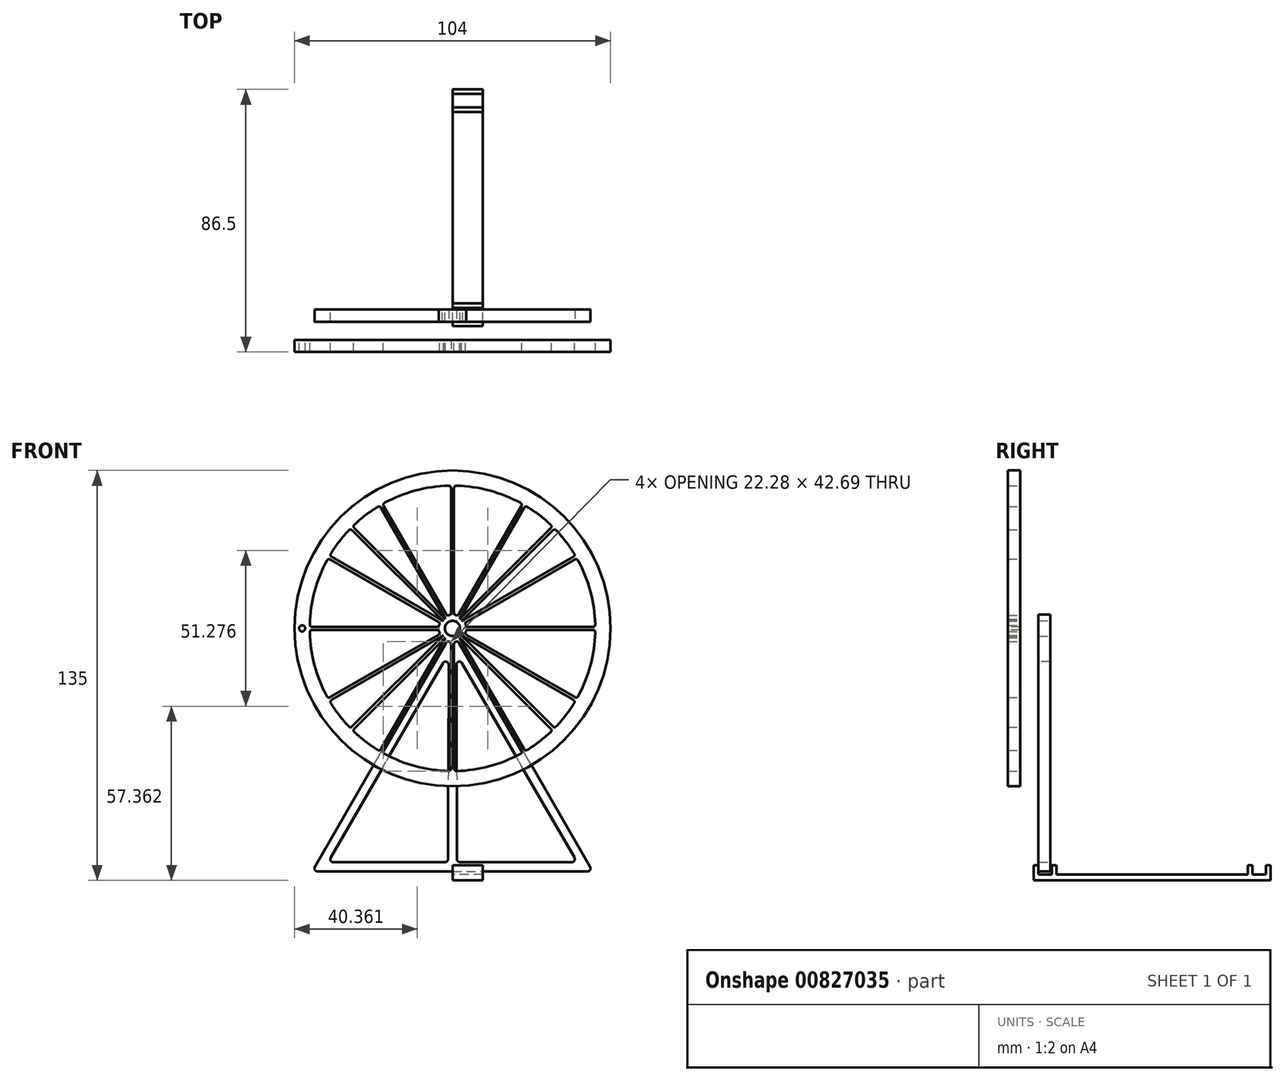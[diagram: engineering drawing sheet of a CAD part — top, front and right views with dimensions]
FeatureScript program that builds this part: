
annotation { "Feature Type Name" : "Feature", "Feature Type Description" : "" }
export const myFeature = defineFeature(function(context is Context, id is Id, definition is map)
    precondition{}
    {
        {
            var Q0;
            Q0=qCreatedBy(makeId("Front.planeOp"),FACE);
            var sketch = newSketch(context, id + "F0", { "sketchPlane" : qUnion([Q0])});
            skCircle(sketch, "E0", {"center": v(0, 0) * mm, "radius": 52 * mm});
            skCircle(sketch, "E1.0", {"center": v(0, 0) * mm, "radius": 47 * mm});
            skLineSegment(sketch, "E2", {"start": v(0, 0) * mm, "end": v(0, 47) * mm});
            skLineSegment(sketch, "E3", {"start": v(0, 0) * mm, "end": v(47, 0) * mm});
            skLineSegment(sketch, "E4", {"start": v(0, 0) * mm, "end": v(23.5, 40.7) * mm});
            skPoint(sketch, "E4.endSnap0", {"position": v(23.5, 0) * mm});
            skLineSegment(sketch, "E5", {"start": v(0, 0) * mm, "end": v(40.7, 23.5) * mm});
            skPoint(sketch, "E5.endSnap0", {"position": v(0, 23.5) * mm});
            skLineSegment(sketch, "E6", {"start": v(0, 0) * mm, "end": v(33.23, 33.23) * mm});
            skLineSegment(sketch, "E7.0", {"start": v(0.5, 1.87) * mm, "end": v(23.07, 40.95) * mm});
            skLineSegment(sketch, "E7.1", {"start": v(0.5, 1.87) * mm, "end": v(0.5, 23) * mm});
            skLineSegment(sketch, "E8.0", {"start": v(2.33, 3.04) * mm, "end": v(23.93, 40.45) * mm});
            skLineSegment(sketch, "E8.1", {"start": v(2.33, 3.04) * mm, "end": v(15.9, 16.62) * mm});
            skLineSegment(sketch, "E9.0", {"start": v(3.04, 2.33) * mm, "end": v(16.62, 15.9) * mm});
            skLineSegment(sketch, "E9.1", {"start": v(3.04, 2.33) * mm, "end": v(40.45, 23.93) * mm});
            skLineSegment(sketch, "E10.0", {"start": v(1.87, 0.5) * mm, "end": v(40.95, 23.07) * mm});
            skLineSegment(sketch, "E10.1", {"start": v(1.87, 0.5) * mm, "end": v(23, 0.5) * mm});
            skLineSegment(sketch, "E11.1.0", {"start": v(-2.31, 3.03) * mm, "end": v(-15.89, 16.6) * mm});
            skLineSegment(sketch, "E11.1.1", {"start": v(-3.02, 2.32) * mm, "end": v(-16.6, 15.9) * mm});
            skLineSegment(sketch, "E11.1.2", {"start": v(0.02, -0.01) * mm, "end": v(-23.48, 40.7) * mm});
            skLineSegment(sketch, "E11.1.3", {"start": v(-3.02, 2.32) * mm, "end": v(-40.43, 23.92) * mm});
            skLineSegment(sketch, "E11.1.4", {"start": v(0.02, -0.01) * mm, "end": v(-40.68, 23.49) * mm});
            skLineSegment(sketch, "E11.1.5", {"start": v(-1.85, 0.49) * mm, "end": v(-22.98, 0.49) * mm});
            skLineSegment(sketch, "E11.1.6", {"start": v(-0.48, 1.86) * mm, "end": v(-0.48, 22.99) * mm});
            skLineSegment(sketch, "E11.1.7", {"start": v(0.02, -0.01) * mm, "end": v(-33.21, 33.22) * mm});
            skLineSegment(sketch, "E11.1.8", {"start": v(-0.48, 1.86) * mm, "end": v(-23.05, 40.94) * mm});
            skLineSegment(sketch, "E11.1.9", {"start": v(-2.31, 3.03) * mm, "end": v(-23.91, 40.44) * mm});
            skLineSegment(sketch, "E11.1.10", {"start": v(-1.85, 0.49) * mm, "end": v(-40.93, 23.06) * mm});
            skLineSegment(sketch, "E11.2.0", {"start": v(-3, -2.32) * mm, "end": v(-16.59, -15.9) * mm});
            skLineSegment(sketch, "E11.2.1", {"start": v(-2.3, -3.03) * mm, "end": v(-15.88, -16.6) * mm});
            skLineSegment(sketch, "E11.2.2", {"start": v(0.03, 0.01) * mm, "end": v(-40.67, -23.49) * mm});
            skLineSegment(sketch, "E11.2.3", {"start": v(-2.3, -3.03) * mm, "end": v(-23.9, -40.44) * mm});
            skLineSegment(sketch, "E11.2.4", {"start": v(0.03, 0.01) * mm, "end": v(-23.47, -40.7) * mm});
            skLineSegment(sketch, "E11.2.5", {"start": v(-0.47, -1.86) * mm, "end": v(-0.47, -22.99) * mm});
            skLineSegment(sketch, "E11.2.6", {"start": v(-1.83, -0.49) * mm, "end": v(-22.97, -0.49) * mm});
            skLineSegment(sketch, "E11.2.7", {"start": v(0.03, 0.01) * mm, "end": v(-33.2, -33.22) * mm});
            skLineSegment(sketch, "E11.2.8", {"start": v(-1.83, -0.49) * mm, "end": v(-40.92, -23.06) * mm});
            skLineSegment(sketch, "E11.2.9", {"start": v(-3, -2.32) * mm, "end": v(-40.42, -23.92) * mm});
            skLineSegment(sketch, "E11.2.10", {"start": v(-0.47, -1.86) * mm, "end": v(-23.04, -40.94) * mm});
            skPoint(sketch, "E11.center", {"position": v(0.02, 0) * mm});
            skCircle(sketch, "E12", {"center": v(0, 0) * mm, "radius": 2.5 * mm});
            skLineSegment(sketch, "E13.0", {"start": v(-0.35, 0.35) * mm, "end": v(33.59, 34.3) * mm});
            skLineSegment(sketch, "E14.0", {"start": v(0.35, -0.35) * mm, "end": v(34.3, 33.59) * mm});
            skLineSegment(sketch, "E15.0", {"start": v(0, -0.5) * mm, "end": v(48, -0.5) * mm});
            skLineSegment(sketch, "E16.0", {"start": v(0.5, 0) * mm, "end": v(0.5, 48) * mm});
            skLineSegment(sketch, "E17.MirrorCS", {"start": v(0, 0.5) * mm, "end": v(48, 0.5) * mm});
            skLineSegment(sketch, "E18.3.3.0", {"start": v(3.05, -2.31) * mm, "end": v(16.63, -15.89) * mm});
            skLineSegment(sketch, "E18.6.3.0", {"start": v(0.01, 0.02) * mm, "end": v(23.51, -40.68) * mm});
            skLineSegment(sketch, "E18.9.3.0", {"start": v(3.05, -2.31) * mm, "end": v(40.46, -23.91) * mm});
            skLineSegment(sketch, "E18.12.3.0", {"start": v(0.01, 0.02) * mm, "end": v(40.71, -23.48) * mm});
            skLineSegment(sketch, "E18.15.3.0", {"start": v(1.88, -0.48) * mm, "end": v(23.01, -0.48) * mm});
            skLineSegment(sketch, "E18.16.3.0", {"start": v(2.34, -3.02) * mm, "end": v(15.92, -16.6) * mm});
            skLineSegment(sketch, "E18.18.3.0", {"start": v(0.51, -1.85) * mm, "end": v(0.51, -22.98) * mm});
            skLineSegment(sketch, "E18.21.3.0", {"start": v(0.01, 0.02) * mm, "end": v(33.24, -33.21) * mm});
            skLineSegment(sketch, "E18.24.3.0", {"start": v(0.51, -1.85) * mm, "end": v(23.08, -40.93) * mm});
            skLineSegment(sketch, "E18.27.3.0", {"start": v(2.34, -3.02) * mm, "end": v(23.94, -40.43) * mm});
            skLineSegment(sketch, "E18.30.3.0", {"start": v(1.88, -0.48) * mm, "end": v(40.96, -23.05) * mm});
            skLineSegment(sketch, "E19", {"start": v(-15.89, 16.6) * mm, "end": v(-32.87, 33.6) * mm});
            skLineSegment(sketch, "E20", {"start": v(-16.6, 15.9) * mm, "end": v(-33.58, 32.88) * mm});
            skLineSegment(sketch, "E21", {"start": v(-22.98, 0.49) * mm, "end": v(-47, 0.49) * mm});
            skLineSegment(sketch, "E22", {"start": v(-22.97, -0.49) * mm, "end": v(-47, -0.49) * mm});
            skLineSegment(sketch, "E23", {"start": v(-16.59, -15.9) * mm, "end": v(-33.58, -32.89) * mm});
            skLineSegment(sketch, "E24", {"start": v(-15.88, -16.6) * mm, "end": v(-32.87, -33.6) * mm});
            skLineSegment(sketch, "E25", {"start": v(-0.47, -22.99) * mm, "end": v(-0.47, -47) * mm});
            skLineSegment(sketch, "E26", {"start": v(0.51, -22.98) * mm, "end": v(0.51, -47) * mm});
            skLineSegment(sketch, "E27", {"start": v(15.92, -16.6) * mm, "end": v(32.9, -33.57) * mm});
            skLineSegment(sketch, "E28", {"start": v(16.63, -15.89) * mm, "end": v(33.6, -32.86) * mm});
            skLineSegment(sketch, "E29", {"start": v(-0.48, 22.99) * mm, "end": v(-0.48, 47) * mm});
            skCircle(sketch, "E30.0", {"center": v(0, 0) * mm, "radius": 4.5 * mm});
            skSolve(sketch);
        }
        {
            var Q0;
            {var subQ0=sQuery(id+"F0.wireOp",EDGE,"E4");var subQ1=sQuery(id+"F0.wireOp",EDGE,"E1.0");var subQ2=makeQuery(id+"F0.imprint","INTERSECT",VERTEX,{"derivedFrom":[subQ1,subQ0]});Q0=makeQuery(id+"F0.imprint","IMPRINT",FACE,{"disambiguationData":[TD([[makeQuery(id+"F0.imprint","IMPRINT",EDGE,{"disambiguationData":[TD([[subQ2,-1.0]])],"derivedFrom":subQ1}),1.0]])]});}
            var Q1;
            {var subQ0=sQuery(id+"F0.wireOp",EDGE,"E8.0");var subQ1=sQuery(id+"F0.wireOp",EDGE,"E1.0");var subQ2=makeQuery(id+"F0.imprint","INTERSECT",VERTEX,{"derivedFrom":[subQ1,subQ0]});Q1=makeQuery(id+"F0.imprint","IMPRINT",FACE,{"disambiguationData":[TD([[makeQuery(id+"F0.imprint","IMPRINT",EDGE,{"disambiguationData":[TD([[subQ2,-1.0]])],"derivedFrom":subQ1}),1.0]])]});}
            var Q2;
            {var subQ5=sQuery(id+"F0.wireOp",EDGE,"E6");var subQ7=sQuery(id+"F0.wireOp",EDGE,"E1.0");var subQ8=makeQuery(id+"F0.imprint","INTERSECT",VERTEX,{"derivedFrom":[subQ7,subQ5]});Q2=makeQuery(id+"F0.imprint","IMPRINT",FACE,{"disambiguationData":[TD([[makeQuery(id+"F0.imprint","IMPRINT",EDGE,{"disambiguationData":[TD([[subQ8,-1.0]])],"derivedFrom":subQ7}),1.0]])]});}
            var Q3;
            {var subQ0=sQuery(id+"F0.wireOp",EDGE,"E14.0");var subQ3=sQuery(id+"F0.wireOp",EDGE,"E1.0");var subQ4=makeQuery(id+"F0.imprint","INTERSECT",VERTEX,{"derivedFrom":[subQ3,subQ0]});Q3=makeQuery(id+"F0.imprint","IMPRINT",FACE,{"disambiguationData":[TD([[makeQuery(id+"F0.imprint","IMPRINT",EDGE,{"disambiguationData":[TD([[subQ4,-1.0]])],"derivedFrom":subQ3}),1.0]])]});}
            var Q4;
            {var subQ0=sQuery(id+"F0.wireOp",EDGE,"E30.0");var subQ1=sQuery(id+"F0.wireOp",EDGE,"E4");var subQ2=makeQuery(id+"F0.imprint","INTERSECT",VERTEX,{"derivedFrom":[subQ1,subQ0]});Q4=makeQuery(id+"F0.imprint","IMPRINT",FACE,{"disambiguationData":[TD([[makeQuery(id+"F0.imprint","IMPRINT",EDGE,{"disambiguationData":[TD([[subQ2,1.0]])],"derivedFrom":subQ1}),1.0]])]});}
            var Q5;
            {var subQ0=sQuery(id+"F0.wireOp",EDGE,"E30.0");var subQ1=sQuery(id+"F0.wireOp",EDGE,"E5");var subQ2=makeQuery(id+"F0.imprint","INTERSECT",VERTEX,{"derivedFrom":[subQ1,subQ0]});Q5=makeQuery(id+"F0.imprint","IMPRINT",FACE,{"disambiguationData":[TD([[makeQuery(id+"F0.imprint","IMPRINT",EDGE,{"disambiguationData":[TD([[subQ2,1.0]])],"derivedFrom":subQ1}),-1.0]])]});}
            var Q6;
            {var subQ0=sQuery(id+"F0.wireOp",EDGE,"E10.0");var subQ1=sQuery(id+"F0.wireOp",EDGE,"E1.0");var subQ2=makeQuery(id+"F0.imprint","INTERSECT",VERTEX,{"derivedFrom":[subQ1,subQ0]});Q6=makeQuery(id+"F0.imprint","IMPRINT",FACE,{"disambiguationData":[TD([[makeQuery(id+"F0.imprint","IMPRINT",EDGE,{"disambiguationData":[TD([[subQ2,-1.0]])],"derivedFrom":subQ1}),1.0]])]});}
            var Q7;
            {var subQ0=sQuery(id+"F0.wireOp",EDGE,"E5");var subQ1=sQuery(id+"F0.wireOp",EDGE,"E1.0");var subQ2=makeQuery(id+"F0.imprint","INTERSECT",VERTEX,{"derivedFrom":[subQ1,subQ0]});Q7=makeQuery(id+"F0.imprint","IMPRINT",FACE,{"disambiguationData":[TD([[makeQuery(id+"F0.imprint","IMPRINT",EDGE,{"disambiguationData":[TD([[subQ2,-1.0]])],"derivedFrom":subQ1}),1.0]])]});}
            var Q8;
            {var subQ3=sQuery(id+"F0.wireOp",EDGE,"E16.0");var subQ5=sQuery(id+"F0.wireOp",EDGE,"E1.0");var subQ6=makeQuery(id+"F0.imprint","INTERSECT",VERTEX,{"derivedFrom":[subQ5,subQ3]});Q8=makeQuery(id+"F0.imprint","IMPRINT",FACE,{"disambiguationData":[TD([[makeQuery(id+"F0.imprint","IMPRINT",EDGE,{"disambiguationData":[TD([[subQ6,-1.0]])],"derivedFrom":subQ5}),1.0]])]});}
            var Q9;
            {var subQ3=sQuery(id+"F0.wireOp",EDGE,"E1.0");var subQ7=sQuery(id+"F0.wireOp",EDGE,"E3");var subQ9=makeQuery(id+"F0.imprint","INTERSECT",VERTEX,{"derivedFrom":[subQ3,subQ7]});Q9=makeQuery(id+"F0.imprint","IMPRINT",FACE,{"disambiguationData":[TD([[makeQuery(id+"F0.imprint","IMPRINT",EDGE,{"disambiguationData":[TD([[subQ9,-1.0]])],"derivedFrom":subQ3}),1.0]])]});}
            var Q10;
            Q10=makeQuery(id+"F0.imprint","IMPRINT",FACE,{"disambiguationData":[TD([[makeQuery(id+"F0.imprint","IMPRINT",EDGE,{"derivedFrom":sQuery(id+"F0.wireOp",EDGE,"E0")}),1.0]])]});
            var Q11;
            {var subQ0=sQuery(id+"F0.wireOp",EDGE,"E30.0");var subQ1=sQuery(id+"F0.wireOp",EDGE,"E2");var subQ2=makeQuery(id+"F0.imprint","INTERSECT",VERTEX,{"derivedFrom":[subQ1,subQ0]});Q11=makeQuery(id+"F0.imprint","IMPRINT",FACE,{"disambiguationData":[TD([[makeQuery(id+"F0.imprint","IMPRINT",EDGE,{"disambiguationData":[TD([[subQ2,1.0]])],"derivedFrom":subQ1}),-1.0]])]});}
            var Q12;
            {var subQ5=sQuery(id+"F0.wireOp",EDGE,"E6");var subQ7=sQuery(id+"F0.wireOp",EDGE,"E30.0");var subQ8=makeQuery(id+"F0.imprint","INTERSECT",VERTEX,{"derivedFrom":[subQ5,subQ7]});Q12=makeQuery(id+"F0.imprint","IMPRINT",FACE,{"disambiguationData":[TD([[makeQuery(id+"F0.imprint","IMPRINT",EDGE,{"disambiguationData":[TD([[subQ8,1.0]])],"derivedFrom":subQ5}),-1.0]])]});}
            var Q13;
            {var subQ0=sQuery(id+"F0.wireOp",EDGE,"E30.0");var subQ1=sQuery(id+"F0.wireOp",EDGE,"E10.0");var subQ2=makeQuery(id+"F0.imprint","INTERSECT",VERTEX,{"derivedFrom":[subQ1,subQ0]});Q13=makeQuery(id+"F0.imprint","IMPRINT",FACE,{"disambiguationData":[TD([[makeQuery(id+"F0.imprint","IMPRINT",EDGE,{"disambiguationData":[TD([[subQ2,1.0]])],"derivedFrom":subQ1}),-1.0]])]});}
            var Q14;
            {var subQ0=sQuery(id+"F0.wireOp",EDGE,"E30.0");var subQ1=sQuery(id+"F0.wireOp",EDGE,"E3");var subQ2=makeQuery(id+"F0.imprint","INTERSECT",VERTEX,{"derivedFrom":[subQ1,subQ0]});Q14=makeQuery(id+"F0.imprint","IMPRINT",FACE,{"disambiguationData":[TD([[makeQuery(id+"F0.imprint","IMPRINT",EDGE,{"disambiguationData":[TD([[subQ2,1.0]])],"derivedFrom":subQ1}),1.0]])]});}
            var Q15;
            {var subQ5=sQuery(id+"F0.wireOp",EDGE,"E5");var subQ7=sQuery(id+"F0.wireOp",EDGE,"E30.0");var subQ8=makeQuery(id+"F0.imprint","INTERSECT",VERTEX,{"derivedFrom":[subQ5,subQ7]});Q15=makeQuery(id+"F0.imprint","IMPRINT",FACE,{"disambiguationData":[TD([[makeQuery(id+"F0.imprint","IMPRINT",EDGE,{"disambiguationData":[TD([[subQ8,1.0]])],"derivedFrom":subQ5}),1.0]])]});}
            var Q16;
            {var subQ5=sQuery(id+"F0.wireOp",EDGE,"E30.0");var subQ6=sQuery(id+"F0.wireOp",EDGE,"E6");var subQ7=makeQuery(id+"F0.imprint","INTERSECT",VERTEX,{"derivedFrom":[subQ6,subQ5]});Q16=makeQuery(id+"F0.imprint","IMPRINT",FACE,{"disambiguationData":[TD([[makeQuery(id+"F0.imprint","IMPRINT",EDGE,{"disambiguationData":[TD([[subQ7,1.0]])],"derivedFrom":subQ6}),1.0]])]});}
            var Q17;
            {var subQ5=sQuery(id+"F0.wireOp",EDGE,"E4");var subQ7=sQuery(id+"F0.wireOp",EDGE,"E30.0");var subQ8=makeQuery(id+"F0.imprint","INTERSECT",VERTEX,{"derivedFrom":[subQ5,subQ7]});Q17=makeQuery(id+"F0.imprint","IMPRINT",FACE,{"disambiguationData":[TD([[makeQuery(id+"F0.imprint","IMPRINT",EDGE,{"disambiguationData":[TD([[subQ8,1.0]])],"derivedFrom":subQ5}),-1.0]])]});}
            var Q18;
            {var subQ0=sQuery(id+"F0.wireOp",EDGE,"E30.0");var subQ1=sQuery(id+"F0.wireOp",EDGE,"E7.0");var subQ2=makeQuery(id+"F0.imprint","INTERSECT",VERTEX,{"derivedFrom":[subQ1,subQ0]});Q18=makeQuery(id+"F0.imprint","IMPRINT",FACE,{"disambiguationData":[TD([[makeQuery(id+"F0.imprint","IMPRINT",EDGE,{"disambiguationData":[TD([[subQ2,1.0]])],"derivedFrom":subQ1}),1.0]])]});}
            extrude(context, id + "F1", {"entities" : qUnion([Q0, Q1, Q2, Q3, Q4, Q5, Q6, Q7, Q8, Q9, Q10, Q11, Q12, Q13, Q14, Q15, Q16, Q17, Q18]), "depth" : 4 * mm, "offsetDistance" : 25 * mm});
        }
        {
            var Q0;
            {var subQ0=sQuery(id+"F0.wireOp",EDGE,"E30.0");var subQ1=sQuery(id+"F0.wireOp",EDGE,"E10.0");var subQ2=sQuery(id+"F0.wireOp",EDGE,"E1.0");Q0=qUnion([makeQuery(id+"F1.opExtrude","SWEPT_EDGE",EDGE,{"disambiguationData":[OSD([sQuery(id+"F0.wireOp",EDGE,"E10.1"),subQ0])]}),makeQuery(id+"F1.opExtrude","SWEPT_EDGE",EDGE,{"disambiguationData":[OSD([subQ2,sQuery(id+"F0.wireOp",EDGE,"E17.MirrorCS")])]}),makeQuery(id+"F1.opExtrude","SWEPT_EDGE",EDGE,{"disambiguationData":[OSD([subQ2,subQ1])]}),makeQuery(id+"F1.opExtrude","SWEPT_EDGE",EDGE,{"disambiguationData":[OSD([subQ1,subQ0])]})]);}
            var Q1;
            {var subQ0=sQuery(id+"F0.wireOp",EDGE,"E1.0");var subQ1=sQuery(id+"F0.wireOp",EDGE,"E30.0");var subQ2=sQuery(id+"F0.wireOp",EDGE,"E7.0");Q1=qUnion([makeQuery(id+"F1.opExtrude","SWEPT_EDGE",EDGE,{"disambiguationData":[OSD([subQ2,subQ1])]}),makeQuery(id+"F1.opExtrude","SWEPT_EDGE",EDGE,{"disambiguationData":[OSD([subQ0,subQ2])]}),makeQuery(id+"F1.opExtrude","SWEPT_EDGE",EDGE,{"disambiguationData":[OSD([sQuery(id+"F0.wireOp",EDGE,"E7.1"),subQ1])]}),makeQuery(id+"F1.opExtrude","SWEPT_EDGE",EDGE,{"disambiguationData":[OSD([subQ0,sQuery(id+"F0.wireOp",EDGE,"E16.0")])]})]);}
            var Q2;
            Q2=makeQuery(id+"F1.opExtrude","SWEPT_EDGE",EDGE,{"disambiguationData":[OSD([sQuery(id+"F0.wireOp",EDGE,"E1.0"),sQuery(id+"F0.wireOp",EDGE,"E7.0")])]});
            var Q3;
            Q3=makeQuery(id+"F1.opExtrude","SWEPT_EDGE",EDGE,{"disambiguationData":[OSD([sQuery(id+"F0.wireOp",EDGE,"E1.0"),sQuery(id+"F0.wireOp",EDGE,"E8.0")])]});
            var Q4;
            Q4=makeQuery(id+"F1.opExtrude","SWEPT_EDGE",EDGE,{"disambiguationData":[OSD([sQuery(id+"F0.wireOp",EDGE,"E1.0"),sQuery(id+"F0.wireOp",EDGE,"E14.0")])]});
            var Q5;
            Q5=makeQuery(id+"F1.opExtrude","SWEPT_EDGE",EDGE,{"disambiguationData":[OSD([sQuery(id+"F0.wireOp",EDGE,"E1.0"),sQuery(id+"F0.wireOp",EDGE,"E10.0")])]});
            var Q6;
            Q6=makeQuery(id+"F1.opExtrude","SWEPT_EDGE",EDGE,{"disambiguationData":[OSD([sQuery(id+"F0.wireOp",EDGE,"E1.0"),sQuery(id+"F0.wireOp",EDGE,"E16.0")])]});
            var Q7;
            Q7=makeQuery(id+"F1.opExtrude","SWEPT_EDGE",EDGE,{"disambiguationData":[OSD([sQuery(id+"F0.wireOp",EDGE,"E1.0"),sQuery(id+"F0.wireOp",EDGE,"E13.0")])]});
            var Q8;
            Q8=makeQuery(id+"F1.opExtrude","SWEPT_EDGE",EDGE,{"disambiguationData":[OSD([sQuery(id+"F0.wireOp",EDGE,"E1.0"),sQuery(id+"F0.wireOp",EDGE,"E9.1")])]});
            var Q9;
            Q9=makeQuery(id+"F1.opExtrude","SWEPT_EDGE",EDGE,{"disambiguationData":[OSD([sQuery(id+"F0.wireOp",EDGE,"E1.0"),sQuery(id+"F0.wireOp",EDGE,"E17.MirrorCS")])]});
            fillet(context, id + "F2", {"entities" : qUnion([Q0, Q1, Q2, Q3, Q4, Q5, Q6, Q7, Q8, Q9]), "radius" : 0.76 * mm, "tangentPropagation" : true, "allowEdgeOverflow" : false});
        }
        {
            var Q0;
            Q0=makeQuery(id+"F1.opExtrude","SWEPT_BODY",BODY,{"disambiguationData":[OSD([sQuery(id+"F0.wireOp",EDGE,"E0"),sQuery(id+"F0.wireOp",EDGE,"E1.0"),sQuery(id+"F0.wireOp",EDGE,"E2"),sQuery(id+"F0.wireOp",EDGE,"E3"),sQuery(id+"F0.wireOp",EDGE,"E7.0"),sQuery(id+"F0.wireOp",EDGE,"E7.1"),sQuery(id+"F0.wireOp",EDGE,"E8.0"),sQuery(id+"F0.wireOp",EDGE,"E8.1"),sQuery(id+"F0.wireOp",EDGE,"E9.0"),sQuery(id+"F0.wireOp",EDGE,"E9.1"),sQuery(id+"F0.wireOp",EDGE,"E10.0"),sQuery(id+"F0.wireOp",EDGE,"E10.1"),sQuery(id+"F0.wireOp",EDGE,"E12"),sQuery(id+"F0.wireOp",EDGE,"E13.0"),sQuery(id+"F0.wireOp",EDGE,"E14.0"),sQuery(id+"F0.wireOp",EDGE,"E16.0"),sQuery(id+"F0.wireOp",EDGE,"E17.MirrorCS"),sQuery(id+"F0.wireOp",EDGE,"E30.0")])]});
            var Q1;
            Q1=makeQuery(id+"F1.opExtrude","SWEPT_FACE",FACE,{"disambiguationData":[OSD([sQuery(id+"F0.wireOp",EDGE,"E12")])]});
            circularPattern(context, id + "F3", {"entities" : qUnion([Q0]), "axis" : qUnion([Q1]), "angle" : 360 * degree, "instanceCount" : 4, "equalSpace" : true});
        }
        {
            var Q0;
            Q0=makeQuery(id+"F1.opExtrude","SWEPT_BODY",BODY,{"disambiguationData":[OSD([sQuery(id+"F0.wireOp",EDGE,"E0"),sQuery(id+"F0.wireOp",EDGE,"E1.0"),sQuery(id+"F0.wireOp",EDGE,"E2"),sQuery(id+"F0.wireOp",EDGE,"E3"),sQuery(id+"F0.wireOp",EDGE,"E7.0"),sQuery(id+"F0.wireOp",EDGE,"E7.1"),sQuery(id+"F0.wireOp",EDGE,"E8.0"),sQuery(id+"F0.wireOp",EDGE,"E8.1"),sQuery(id+"F0.wireOp",EDGE,"E9.0"),sQuery(id+"F0.wireOp",EDGE,"E9.1"),sQuery(id+"F0.wireOp",EDGE,"E10.0"),sQuery(id+"F0.wireOp",EDGE,"E10.1"),sQuery(id+"F0.wireOp",EDGE,"E12"),sQuery(id+"F0.wireOp",EDGE,"E13.0"),sQuery(id+"F0.wireOp",EDGE,"E14.0"),sQuery(id+"F0.wireOp",EDGE,"E16.0"),sQuery(id+"F0.wireOp",EDGE,"E17.MirrorCS"),sQuery(id+"F0.wireOp",EDGE,"E30.0")])]});
            var Q1;
            Q1=makeQuery(id+"F3.opPattern","COPY",BODY,{"derivedFrom":makeQuery(id+"F1.opExtrude","SWEPT_BODY",BODY,{"disambiguationData":[OSD([sQuery(id+"F0.wireOp",EDGE,"E0"),sQuery(id+"F0.wireOp",EDGE,"E1.0"),sQuery(id+"F0.wireOp",EDGE,"E2"),sQuery(id+"F0.wireOp",EDGE,"E3"),sQuery(id+"F0.wireOp",EDGE,"E7.0"),sQuery(id+"F0.wireOp",EDGE,"E7.1"),sQuery(id+"F0.wireOp",EDGE,"E8.0"),sQuery(id+"F0.wireOp",EDGE,"E8.1"),sQuery(id+"F0.wireOp",EDGE,"E9.0"),sQuery(id+"F0.wireOp",EDGE,"E9.1"),sQuery(id+"F0.wireOp",EDGE,"E10.0"),sQuery(id+"F0.wireOp",EDGE,"E10.1"),sQuery(id+"F0.wireOp",EDGE,"E12"),sQuery(id+"F0.wireOp",EDGE,"E13.0"),sQuery(id+"F0.wireOp",EDGE,"E14.0"),sQuery(id+"F0.wireOp",EDGE,"E16.0"),sQuery(id+"F0.wireOp",EDGE,"E17.MirrorCS"),sQuery(id+"F0.wireOp",EDGE,"E30.0")])]}),"instanceName":"1"});
            var Q2;
            Q2=makeQuery(id+"F3.opPattern","COPY",BODY,{"derivedFrom":makeQuery(id+"F1.opExtrude","SWEPT_BODY",BODY,{"disambiguationData":[OSD([sQuery(id+"F0.wireOp",EDGE,"E0"),sQuery(id+"F0.wireOp",EDGE,"E1.0"),sQuery(id+"F0.wireOp",EDGE,"E2"),sQuery(id+"F0.wireOp",EDGE,"E3"),sQuery(id+"F0.wireOp",EDGE,"E7.0"),sQuery(id+"F0.wireOp",EDGE,"E7.1"),sQuery(id+"F0.wireOp",EDGE,"E8.0"),sQuery(id+"F0.wireOp",EDGE,"E8.1"),sQuery(id+"F0.wireOp",EDGE,"E9.0"),sQuery(id+"F0.wireOp",EDGE,"E9.1"),sQuery(id+"F0.wireOp",EDGE,"E10.0"),sQuery(id+"F0.wireOp",EDGE,"E10.1"),sQuery(id+"F0.wireOp",EDGE,"E12"),sQuery(id+"F0.wireOp",EDGE,"E13.0"),sQuery(id+"F0.wireOp",EDGE,"E14.0"),sQuery(id+"F0.wireOp",EDGE,"E16.0"),sQuery(id+"F0.wireOp",EDGE,"E17.MirrorCS"),sQuery(id+"F0.wireOp",EDGE,"E30.0")])]}),"instanceName":"2"});
            var Q3;
            Q3=makeQuery(id+"F3.opPattern","COPY",BODY,{"derivedFrom":makeQuery(id+"F1.opExtrude","SWEPT_BODY",BODY,{"disambiguationData":[OSD([sQuery(id+"F0.wireOp",EDGE,"E0"),sQuery(id+"F0.wireOp",EDGE,"E1.0"),sQuery(id+"F0.wireOp",EDGE,"E2"),sQuery(id+"F0.wireOp",EDGE,"E3"),sQuery(id+"F0.wireOp",EDGE,"E7.0"),sQuery(id+"F0.wireOp",EDGE,"E7.1"),sQuery(id+"F0.wireOp",EDGE,"E8.0"),sQuery(id+"F0.wireOp",EDGE,"E8.1"),sQuery(id+"F0.wireOp",EDGE,"E9.0"),sQuery(id+"F0.wireOp",EDGE,"E9.1"),sQuery(id+"F0.wireOp",EDGE,"E10.0"),sQuery(id+"F0.wireOp",EDGE,"E10.1"),sQuery(id+"F0.wireOp",EDGE,"E12"),sQuery(id+"F0.wireOp",EDGE,"E13.0"),sQuery(id+"F0.wireOp",EDGE,"E14.0"),sQuery(id+"F0.wireOp",EDGE,"E16.0"),sQuery(id+"F0.wireOp",EDGE,"E17.MirrorCS"),sQuery(id+"F0.wireOp",EDGE,"E30.0")])]}),"instanceName":"3"});
            booleanBodies(context, id + "F4", {"operationType" : BooleanOperationType.UNION, "tools" : qUnion([Q0, Q1, Q2, Q3])});
        }
        {
            var Q0;
            Q0=qCreatedBy(makeId("Front.planeOp"),FACE);
            cPlane(context, id + "F5", {"entities" : qUnion([Q0]), "cplaneType" : CPlaneType.OFFSET, "offset" : 10 * mm, "oppositeDirection" : true, "width" : 150 * mm, "height" : 150 * mm});
        }
        {
            var Q0;
            Q0=qCreatedBy(id+"F5.planeOp",FACE);
            var sketch = newSketch(context, id + "F6", { "sketchPlane" : qUnion([Q0])});
            skCircle(sketch, "E31", {"center": v(0, 0) * mm, "radius": 2.5 * mm});
            skCircle(sketch, "E32", {"center": v(0, 0) * mm, "radius": 4.5 * mm});
            skLineSegment(sketch, "E33", {"start": v(0, 0) * mm, "end": v(0, -80) * mm});
            skLineSegment(sketch, "E34", {"start": v(0, -80) * mm, "end": v(46.19, -80) * mm});
            skLineSegment(sketch, "E35", {"start": v(46.19, -80) * mm, "end": v(0, 0) * mm});
            skLineSegment(sketch, "E36.0", {"start": v(41, -77) * mm, "end": v(3, -11.2) * mm});
            skLineSegment(sketch, "E36.1", {"start": v(3, -77) * mm, "end": v(41, -77) * mm});
            skLineSegment(sketch, "E36.2", {"start": v(3, -11.2) * mm, "end": v(3, -77) * mm});
            skLineSegment(sketch, "E37.MirrorCS", {"start": v(-46.19, -80) * mm, "end": v(0, 0) * mm});
            skLineSegment(sketch, "E38.MirrorCS", {"start": v(0, -80) * mm, "end": v(-46.19, -80) * mm});
            skLineSegment(sketch, "E39.MirrorCS", {"start": v(-3, -77) * mm, "end": v(-41, -77) * mm});
            skLineSegment(sketch, "E40.MirrorCS", {"start": v(-41, -77) * mm, "end": v(-3, -11.2) * mm});
            skLineSegment(sketch, "E41.MirrorCS", {"start": v(-3, -11.2) * mm, "end": v(-3, -77) * mm});
            skLineSegment(sketch, "E42", {"start": v(-3, -77) * mm, "end": v(-1.5, -77) * mm});
            skLineSegment(sketch, "E43", {"start": v(-1.26, -8.18) * mm, "end": v(-1.5, -77) * mm});
            skLineSegment(sketch, "E44", {"start": v(-3, -11.2) * mm, "end": v(-1.26, -8.18) * mm});
            skLineSegment(sketch, "E45.MirrorCS", {"start": v(3, -11.2) * mm, "end": v(1.26, -8.18) * mm});
            skLineSegment(sketch, "E46.MirrorCS", {"start": v(1.26, -8.18) * mm, "end": v(1.5, -77) * mm});
            skLineSegment(sketch, "E47.MirrorCS", {"start": v(3, -77) * mm, "end": v(1.5, -77) * mm});
            skSolve(sketch);
        }
        {
            var Q0;
            Q0 = qSketchRegion(id + "F6", true);
            extrude(context, id + "F7", {"entities" : qUnion([Q0]), "depth" : 4 * mm, "offsetDistance" : 25 * mm});
        }
        {
            var Q0;
            Q0=makeQuery(id+"F7.opExtrude","SWEPT_EDGE",EDGE,{"disambiguationData":[OSD([sQuery(id+"F6.wireOp",EDGE,"E32"),sQuery(id+"F6.wireOp",EDGE,"E35")])]});
            var Q1;
            Q1=makeQuery(id+"F7.opExtrude","SWEPT_EDGE",EDGE,{"disambiguationData":[OSD([sQuery(id+"F6.wireOp",EDGE,"E32"),sQuery(id+"F6.wireOp",EDGE,"E37.MirrorCS")])]});
            fillet(context, id + "F8", {"entities" : qUnion([Q0, Q1]), "radius" : 5 * mm, "tangentPropagation" : true, "allowEdgeOverflow" : false});
        }
        {
            var Q0;
            Q0=qCreatedBy(makeId("Front.planeOp"),FACE);
            var sketch = newSketch(context, id + "F9", { "sketchPlane" : qUnion([Q0])});
            skLineSegment(sketch, "E48", {"start": v(0, 0) * mm, "end": v(-49.5, 0) * mm});
            skCircle(sketch, "E49", {"center": v(-49.5, 0) * mm, "radius": 1 * mm});
            skSolve(sketch);
        }
        {
            var Q0;
            Q0=makeQuery(id+"FfCFLKiH3RzbdgV_2.18.F9.imprint","IMPRINT",FACE,{"disambiguationData":[TD([[makeQuery(id+"FfCFLKiH3RzbdgV_2.18.F9.imprint","IMPRINT",EDGE,{"derivedFrom":sQuery(id+"FfCFLKiH3RzbdgV_2.18.F9.wireOp",EDGE,"E49")}),1.0]])]});
            var Q1;
            Q1=makeQuery(id+"FfCFLKiH3RzbdgV_2.20.F9.imprint","IMPRINT",FACE,{"disambiguationData":[TD([[makeQuery(id+"FfCFLKiH3RzbdgV_2.20.F9.imprint","IMPRINT",EDGE,{"derivedFrom":sQuery(id+"FfCFLKiH3RzbdgV_2.20.F9.wireOp",EDGE,"E49")}),1.0]])]});
            var Q2;
            Q2=makeQuery(id+"FfCFLKiH3RzbdgV_2.21.F9.imprint","IMPRINT",FACE,{"disambiguationData":[TD([[makeQuery(id+"FfCFLKiH3RzbdgV_2.21.F9.imprint","IMPRINT",EDGE,{"derivedFrom":sQuery(id+"FfCFLKiH3RzbdgV_2.21.F9.wireOp",EDGE,"E49")}),1.0]])]});
            var Q3;
            Q3=makeQuery(id+"FfCFLKiH3RzbdgV_2.22.F9.imprint","IMPRINT",FACE,{"disambiguationData":[TD([[makeQuery(id+"FfCFLKiH3RzbdgV_2.22.F9.imprint","IMPRINT",EDGE,{"derivedFrom":sQuery(id+"FfCFLKiH3RzbdgV_2.22.F9.wireOp",EDGE,"E49")}),1.0]])]});
            var Q4;
            Q4=makeQuery(id+"F9.imprint","IMPRINT",FACE,{"disambiguationData":[TD([[makeQuery(id+"F9.imprint","IMPRINT",EDGE,{"derivedFrom":sQuery(id+"F9.wireOp",EDGE,"E49")}),1.0]])]});
            var Q5;
            Q5=makeQuery(id+"FfCFLKiH3RzbdgV_2.2.F9.imprint","IMPRINT",FACE,{"disambiguationData":[TD([[makeQuery(id+"FfCFLKiH3RzbdgV_2.2.F9.imprint","IMPRINT",EDGE,{"derivedFrom":sQuery(id+"FfCFLKiH3RzbdgV_2.2.F9.wireOp",EDGE,"E49")}),1.0]])]});
            var Q6;
            Q6=makeQuery(id+"FfCFLKiH3RzbdgV_2.3.F9.imprint","IMPRINT",FACE,{"disambiguationData":[TD([[makeQuery(id+"FfCFLKiH3RzbdgV_2.3.F9.imprint","IMPRINT",EDGE,{"derivedFrom":sQuery(id+"FfCFLKiH3RzbdgV_2.3.F9.wireOp",EDGE,"E49")}),1.0]])]});
            var Q7;
            Q7=makeQuery(id+"FfCFLKiH3RzbdgV_2.4.F9.imprint","IMPRINT",FACE,{"disambiguationData":[TD([[makeQuery(id+"FfCFLKiH3RzbdgV_2.4.F9.imprint","IMPRINT",EDGE,{"derivedFrom":sQuery(id+"FfCFLKiH3RzbdgV_2.4.F9.wireOp",EDGE,"E49")}),1.0]])]});
            var Q8;
            Q8=makeQuery(id+"FfCFLKiH3RzbdgV_2.6.F9.imprint","IMPRINT",FACE,{"disambiguationData":[TD([[makeQuery(id+"FfCFLKiH3RzbdgV_2.6.F9.imprint","IMPRINT",EDGE,{"derivedFrom":sQuery(id+"FfCFLKiH3RzbdgV_2.6.F9.wireOp",EDGE,"E49")}),1.0]])]});
            var Q9;
            Q9=makeQuery(id+"FfCFLKiH3RzbdgV_2.8.F9.imprint","IMPRINT",FACE,{"disambiguationData":[TD([[makeQuery(id+"FfCFLKiH3RzbdgV_2.8.F9.imprint","IMPRINT",EDGE,{"derivedFrom":sQuery(id+"FfCFLKiH3RzbdgV_2.8.F9.wireOp",EDGE,"E49")}),1.0]])]});
            var Q10;
            Q10=makeQuery(id+"FfCFLKiH3RzbdgV_2.9.F9.imprint","IMPRINT",FACE,{"disambiguationData":[TD([[makeQuery(id+"FfCFLKiH3RzbdgV_2.9.F9.imprint","IMPRINT",EDGE,{"derivedFrom":sQuery(id+"FfCFLKiH3RzbdgV_2.9.F9.wireOp",EDGE,"E49")}),1.0]])]});
            var Q11;
            Q11=makeQuery(id+"FfCFLKiH3RzbdgV_2.10.F9.imprint","IMPRINT",FACE,{"disambiguationData":[TD([[makeQuery(id+"FfCFLKiH3RzbdgV_2.10.F9.imprint","IMPRINT",EDGE,{"derivedFrom":sQuery(id+"FfCFLKiH3RzbdgV_2.10.F9.wireOp",EDGE,"E49")}),1.0]])]});
            var Q12;
            Q12=makeQuery(id+"FfCFLKiH3RzbdgV_2.12.F9.imprint","IMPRINT",FACE,{"disambiguationData":[TD([[makeQuery(id+"FfCFLKiH3RzbdgV_2.12.F9.imprint","IMPRINT",EDGE,{"derivedFrom":sQuery(id+"FfCFLKiH3RzbdgV_2.12.F9.wireOp",EDGE,"E49")}),1.0]])]});
            var Q13;
            Q13=makeQuery(id+"FfCFLKiH3RzbdgV_2.14.F9.imprint","IMPRINT",FACE,{"disambiguationData":[TD([[makeQuery(id+"FfCFLKiH3RzbdgV_2.14.F9.imprint","IMPRINT",EDGE,{"derivedFrom":sQuery(id+"FfCFLKiH3RzbdgV_2.14.F9.wireOp",EDGE,"E49")}),1.0]])]});
            var Q14;
            Q14=makeQuery(id+"FfCFLKiH3RzbdgV_2.15.F9.imprint","IMPRINT",FACE,{"disambiguationData":[TD([[makeQuery(id+"FfCFLKiH3RzbdgV_2.15.F9.imprint","IMPRINT",EDGE,{"derivedFrom":sQuery(id+"FfCFLKiH3RzbdgV_2.15.F9.wireOp",EDGE,"E49")}),1.0]])]});
            var Q15;
            Q15=makeQuery(id+"FfCFLKiH3RzbdgV_2.16.F9.imprint","IMPRINT",FACE,{"disambiguationData":[TD([[makeQuery(id+"FfCFLKiH3RzbdgV_2.16.F9.imprint","IMPRINT",EDGE,{"derivedFrom":sQuery(id+"FfCFLKiH3RzbdgV_2.16.F9.wireOp",EDGE,"E49")}),1.0]])]});
            extrude(context, id + "F10", {"entities" : qUnion([Q0, Q1, Q2, Q3, Q4, Q5, Q6, Q7, Q8, Q9, Q10, Q11, Q12, Q13, Q14, Q15]), "operationType" : NewBodyOperationType.REMOVE, "depth" : 25 * mm, "offsetDistance" : 25 * mm});
        }
        {
            var Q0;
            Q0=makeQuery(id+"F7.opExtrude","SWEPT_EDGE",EDGE,{"disambiguationData":[OSD([sQuery(id+"F6.wireOp",EDGE,"E34"),sQuery(id+"F6.wireOp",EDGE,"E35")])]});
            var Q1;
            Q1=makeQuery(id+"F7.opExtrude","SWEPT_EDGE",EDGE,{"disambiguationData":[OSD([sQuery(id+"F6.wireOp",EDGE,"E36.0"),sQuery(id+"F6.wireOp",EDGE,"E36.1")])]});
            var Q2;
            Q2=makeQuery(id+"F7.opExtrude","SWEPT_EDGE",EDGE,{"disambiguationData":[OSD([sQuery(id+"F6.wireOp",EDGE,"E46.MirrorCS"),sQuery(id+"F6.wireOp",EDGE,"E47.MirrorCS")])]});
            var Q3;
            Q3=makeQuery(id+"F7.opExtrude","SWEPT_EDGE",EDGE,{"disambiguationData":[OSD([sQuery(id+"F6.wireOp",EDGE,"E42"),sQuery(id+"F6.wireOp",EDGE,"E43")])]});
            var Q4;
            Q4=makeQuery(id+"F7.opExtrude","SWEPT_EDGE",EDGE,{"disambiguationData":[OSD([sQuery(id+"F6.wireOp",EDGE,"E39.MirrorCS"),sQuery(id+"F6.wireOp",EDGE,"E40.MirrorCS")])]});
            var Q5;
            Q5=makeQuery(id+"F7.opExtrude","SWEPT_EDGE",EDGE,{"disambiguationData":[OSD([sQuery(id+"F6.wireOp",EDGE,"E37.MirrorCS"),sQuery(id+"F6.wireOp",EDGE,"E38.MirrorCS")])]});
            var Q6;
            Q6=makeQuery(id+"F7.opExtrude","SWEPT_EDGE",EDGE,{"disambiguationData":[OSD([sQuery(id+"F6.wireOp",EDGE,"E45.MirrorCS"),sQuery(id+"F6.wireOp",EDGE,"E46.MirrorCS")])]});
            var Q7;
            Q7=makeQuery(id+"F7.opExtrude","SWEPT_EDGE",EDGE,{"disambiguationData":[OSD([sQuery(id+"F6.wireOp",EDGE,"E43"),sQuery(id+"F6.wireOp",EDGE,"E44")])]});
            fillet(context, id + "F11", {"entities" : qUnion([Q0, Q1, Q2, Q3, Q4, Q5, Q6, Q7]), "radius" : 1 * mm, "tangentPropagation" : true, "allowEdgeOverflow" : false});
        }
        {
            var Q0;
            Q0=qCreatedBy(makeId("Right.planeOp"),FACE);
            var sketch = newSketch(context, id + "F12", { "sketchPlane" : qUnion([Q0])});
            skLineSegment(sketch, "E50", {"start": v(0, 0) * mm, "end": v(0, -81) * mm});
            skLineSegment(sketch, "E51", {"start": v(0, -81) * mm, "end": v(6, -81) * mm});
            skLineSegment(sketch, "E52", {"start": v(6, -81) * mm, "end": v(81, -81) * mm});
            skLineSegment(sketch, "E53", {"start": v(6, -81) * mm, "end": v(6, -83) * mm});
            skLineSegment(sketch, "E54.bottom", {"start": v(6, -83) * mm, "end": v(81, -83) * mm});
            skLineSegment(sketch, "E54.left", {"start": v(6, -83) * mm, "end": v(6, -81) * mm});
            skLineSegment(sketch, "E54.right", {"start": v(81, -83) * mm, "end": v(81, -81) * mm});
            skLineSegment(sketch, "E55", {"start": v(6, -83) * mm, "end": v(4.5, -83) * mm});
            skLineSegment(sketch, "E56", {"start": v(4.5, -83) * mm, "end": v(4.5, -78) * mm});
            skLineSegment(sketch, "E57.bottom", {"start": v(4.5, -78) * mm, "end": v(6, -78) * mm});
            skLineSegment(sketch, "E57.top", {"start": v(4.5, -81) * mm, "end": v(6, -81) * mm});
            skLineSegment(sketch, "E57.left", {"start": v(4.5, -78) * mm, "end": v(4.5, -81) * mm});
            skLineSegment(sketch, "E57.right", {"start": v(6, -78) * mm, "end": v(6, -81) * mm});
            skLineSegment(sketch, "E58", {"start": v(6, -81) * mm, "end": v(10.5, -81) * mm});
            skLineSegment(sketch, "E59", {"start": v(10.5, -81) * mm, "end": v(10.5, -78) * mm});
            skLineSegment(sketch, "E60", {"start": v(10.5, -78) * mm, "end": v(12, -78) * mm});
            skLineSegment(sketch, "E61", {"start": v(12, -78) * mm, "end": v(12, -81) * mm});
            skLineSegment(sketch, "E62", {"start": v(43.5, -83) * mm, "end": v(43.5, -84.13) * mm});
            skLineSegment(sketch, "E63.MirrorCS", {"start": v(81, -83) * mm, "end": v(82.5, -83) * mm});
            skLineSegment(sketch, "E64.MirrorCS", {"start": v(82.5, -83) * mm, "end": v(82.5, -78) * mm});
            skLineSegment(sketch, "E65.MirrorCS", {"start": v(82.5, -78) * mm, "end": v(81, -78) * mm});
            skLineSegment(sketch, "E66.MirrorCS", {"start": v(81, -78) * mm, "end": v(81, -81) * mm});
            skLineSegment(sketch, "E67.MirrorCS", {"start": v(75, -78) * mm, "end": v(75, -81) * mm});
            skLineSegment(sketch, "E68.MirrorCS", {"start": v(76.5, -78) * mm, "end": v(75, -78) * mm});
            skLineSegment(sketch, "E69.MirrorCS", {"start": v(76.5, -81) * mm, "end": v(76.5, -78) * mm});
            skSolve(sketch);
        }
        {
            var Q0;
            {var subQ3=sQuery(id+"F12.wireOp",EDGE,"E59");var subQ7=sQuery(id+"F12.wireOp",EDGE,"E53");var subQ13=sQuery(id+"F12.wireOp",EDGE,"E54.right");var subQ14=sQuery(id+"F12.wireOp",EDGE,"E67.MirrorCS");var subQ17=makeQuery(id+"F12.imprint","IMPRINT",EDGE,{"derivedFrom":subQ7});var subQ22=makeQuery(id+"F12.imprint","IMPRINT",EDGE,{"derivedFrom":subQ13});var subQ26=sQuery(id+"F12.wireOp",EDGE,"E57.bottom");Q0=qUnion([makeQuery(id+"F12.imprint","IMPRINT",FACE,{"disambiguationData":[TD([[makeQuery(id+"F12.imprint","IMPRINT",EDGE,{"derivedFrom":subQ26}),-1.0]])]}),makeQuery(id+"F12.imprint","IMPRINT",FACE,{"disambiguationData":[TD([[subQ17,-1.0]])]}),makeQuery(id+"F12.imprint","IMPRINT",FACE,{"disambiguationData":[TD([[subQ22,-1.0]])]}),makeQuery(id+"F12.imprint","IMPRINT",FACE,{"disambiguationData":[TD([[makeQuery(id+"F12.imprint","IMPRINT",EDGE,{"derivedFrom":subQ14}),1.0]])]}),makeQuery(id+"F12.imprint","IMPRINT",FACE,{"disambiguationData":[TD([[makeQuery(id+"F12.imprint","IMPRINT",EDGE,{"derivedFrom":subQ3}),-1.0]])]}),makeQuery(id+"F12.imprint","IMPRINT",FACE,{"disambiguationData":[TD([[subQ17,1.0]])]})]);}
            extrude(context, id + "F13", {"entities" : qUnion([Q0]), "depth" : 10 * mm, "offsetDistance" : 25 * mm});
        }
    });
